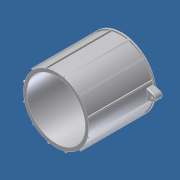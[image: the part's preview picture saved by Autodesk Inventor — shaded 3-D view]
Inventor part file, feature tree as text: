
AUTODESK INVENTOR PART (.ipt)
format: ipt  version: unknown  size: 819,712 bytes
history: native  units: in
note: dims shown in document units (in); Inventor stores cm internally (conversion verified against a paired STEP export)
features: extrude x11, sketch x11, pattern_circular x4, fillet x1, projected_geometry x1
ambient origin geometry x8: Origin, YZ Plane, XZ Plane, XY Plane, X Axis, Y Axis, Z Axis, Center Point
bodies: Solid1 (feature_tree)
feature tree (28):
  extrude  "Extrusion1"  Depth=3.15in
  extrude  "Extrusion2"  Depth=3.0in
  extrude  "Extrusion3"  Depth=3.375in TaperAngle=0.0deg
  extrude  "Extrusion4"  Depth=1.15in
  extrude  "Extrusion5"  Depth=0.05in
  pattern_circular  "Circular Pattern1"  Count=12 Angle=360.0deg
  extrude  "Extrusion6"  Depth=4.7244in TaperAngle=360.0deg
  pattern_circular  "Circular Pattern2"  [2 undecoded]
  extrude  "Extrusion7"  Depth=0.45in TaperAngle=0.0deg
  pattern_circular  "Circular Pattern3"  Count=12 Angle=360.0deg
  extrude  "Extrusion8"  Depth=0.075in
  pattern_circular  "Circular Pattern4"  [2 undecoded]
  extrude  "Extrusion9"  Depth=0.15in TaperAngle=0.0deg
  extrude  "Extrusion10"  Depth=4.7244in TaperAngle=360.0deg
  extrude  "Extrusion11"  Depth=3.7in TaperAngle=0.0deg
  fillet  "Fillet1"  Radius=4.7244in
  sketch  "Sketch1"  dims[d0=3.35in d1=3.15in]
  sketch  "Sketch2"  dims[d2=3.375in d3=0.0in d4=3.0in]
  sketch  "Sketch3"  dims[d5=0.125in d6=0.0in d7=3.375in d8=0.0in]
  sketch  "Sketch4"  dims[d9=0.45in d10=0.0in d11=1.15in]
  sketch  "Sketch5"  dims[d13=0.05in d15=0.05in]
  sketch  "Sketch6"  dims[d16=0.05in d18=4.7244in d20=360.0deg]
  sketch  "Sketch7"  dims[d22=0.075in d23=0.0in d24=4.7244in d25=360.0deg]
  projected_geometry  "Projected Loop1"
  sketch  "Sketch8"  dims[d27=0.1168in]
  sketch  "Sketch9"  dims[d28=0.675in]
  sketch  "Sketch10"  dims[d29=0.2in]
  sketch  "Sketch12"  dims[d30=0.25in d31=0.075in d32=0.45in d33=0.0in d34=4.7244in d35=360.0deg d38=0.075in d39=0.075in d40=0.15in d41=0.0in d42=4.7244in d43=360.0deg d45=3.7in d46=0.0in d47=4.7244in d48=360.0deg d50=0.07in d51=0.0in d52=1.0in d53=0.0in d60=0.375in d61=0.125in d63=0.375in d64=0.0in d65=0.0312in]
note: 4 required parameter values undecoded (feature->parameter linkage not recoverable at this tier; creation-order binding heuristic only, values carry confidence <= 0.55)
